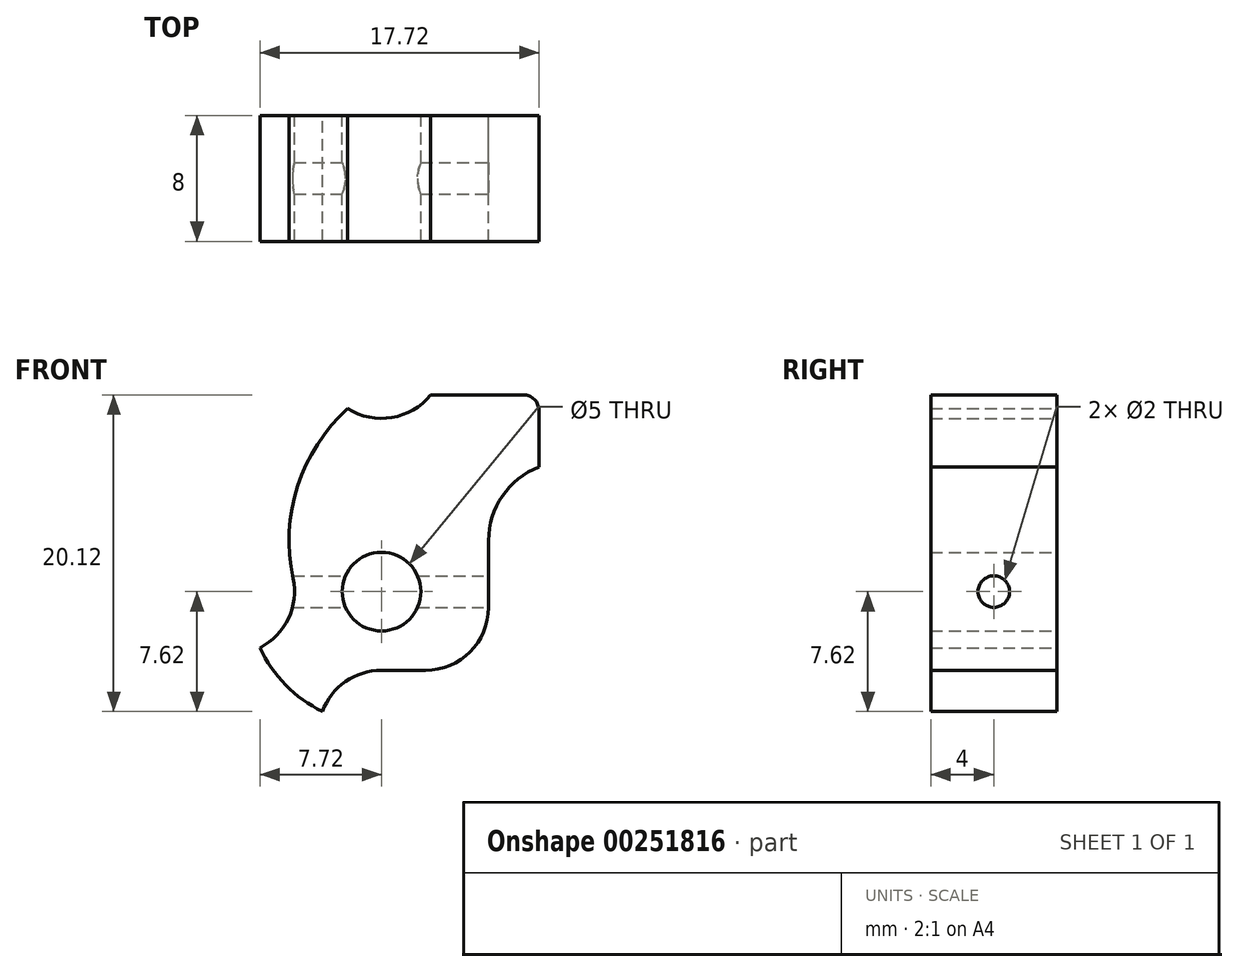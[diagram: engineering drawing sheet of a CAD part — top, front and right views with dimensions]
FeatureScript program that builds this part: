
annotation { "Feature Type Name" : "Feature", "Feature Type Description" : "" }
export const myFeature = defineFeature(function(context is Context, id is Id, definition is map)
    precondition{}
    {
        {
            var Q0;
            Q0=qCreatedBy(makeId("Front.planeOp"),FACE);
            var sketch = newSketch(context, id + "F0", { "sketchPlane" : qUnion([Q0])});
            skCircle(sketch, "E0", {"center": v(0, 0) * mm, "radius": 2.5 * mm});
            skLineSegment(sketch, "E1", {"start": v(0, -5) * mm, "end": v(2.8, -5) * mm});
            skLineSegment(sketch, "E2", {"start": v(6.8, 3.25) * mm, "end": v(6.8, -1) * mm});
            skArc(sketch, "E3", {"start": v(2.8, -5) * mm, "mid": v(5.63, -3.83) * mm, "end": v(6.8, -1) * mm});
            skArc(sketch, "E4", {"start": v(0, -5) * mm, "mid": v(-2.3, -5.72) * mm, "end": v(-3.76, -7.62) * mm});
            skArc(sketch, "E5", {"start": v(-7.72, -3.57) * mm, "mid": v(-6.08, -5.94) * mm, "end": v(-3.76, -7.62) * mm});
            skArc(sketch, "E6", {"start": v(10, 7.91) * mm, "mid": v(7.68, 6.07) * mm, "end": v(6.8, 3.25) * mm});
            skLineSegment(sketch, "E7", {"start": v(10, 7.91) * mm, "end": v(10, 11.5) * mm});
            skLineSegment(sketch, "E8", {"start": v(9, 12.5) * mm, "end": v(3.12, 12.5) * mm});
            skArc(sketch, "E9", {"start": v(-2.15, 11.63) * mm, "mid": v(0.65, 11.05) * mm, "end": v(3.12, 12.5) * mm});
            skArc(sketch, "E10", {"start": v(-7.72, -3.57) * mm, "mid": v(-5.92, -1.72) * mm, "end": v(-5.62, 0.84) * mm});
            skArc(sketch, "E11", {"start": v(-2.15, 11.63) * mm, "mid": v(-5.33, 6.7) * mm, "end": v(-5.62, 0.84) * mm});
            skPoint(sketch, "E12.visualSharp", {"position": v(10, 12.5) * mm});
            skArc(sketch, "E12.filletArc", {"start": v(10, 11.5) * mm, "mid": v(9.7, 12.2) * mm, "end": v(9, 12.5) * mm});
            skSolve(sketch);
        }
        {
            var Q0;
            Q0=makeQuery(id+"F0.imprint","IMPRINT",FACE,{"disambiguationData":[TD([[makeQuery(id+"F0.imprint","IMPRINT",EDGE,{"derivedFrom":sQuery(id+"F0.wireOp",EDGE,"E0")}),-1.0]])]});
            extrude(context, id + "F1", {"entities" : qUnion([Q0]), "endBound" : BoundingType.SYMMETRIC, "depth" : 8 * mm});
        }
        {
            var Q0;
            Q0=qCreatedBy(makeId("Right.planeOp"),FACE);
            var sketch = newSketch(context, id + "F2", { "sketchPlane" : qUnion([Q0])});
            skCircle(sketch, "E13", {"center": v(0, 0) * mm, "radius": 1 * mm});
            skSolve(sketch);
        }
        {
            var Q0;
            Q0 = qSketchRegion(id + "F2", true);
            extrude(context, id + "F3", {"entities" : qUnion([Q0]), "operationType" : NewBodyOperationType.REMOVE, "endBound" : BoundingType.SYMMETRIC, "oppositeDirection" : true, "depth" : 25 * mm});
        }
    });
